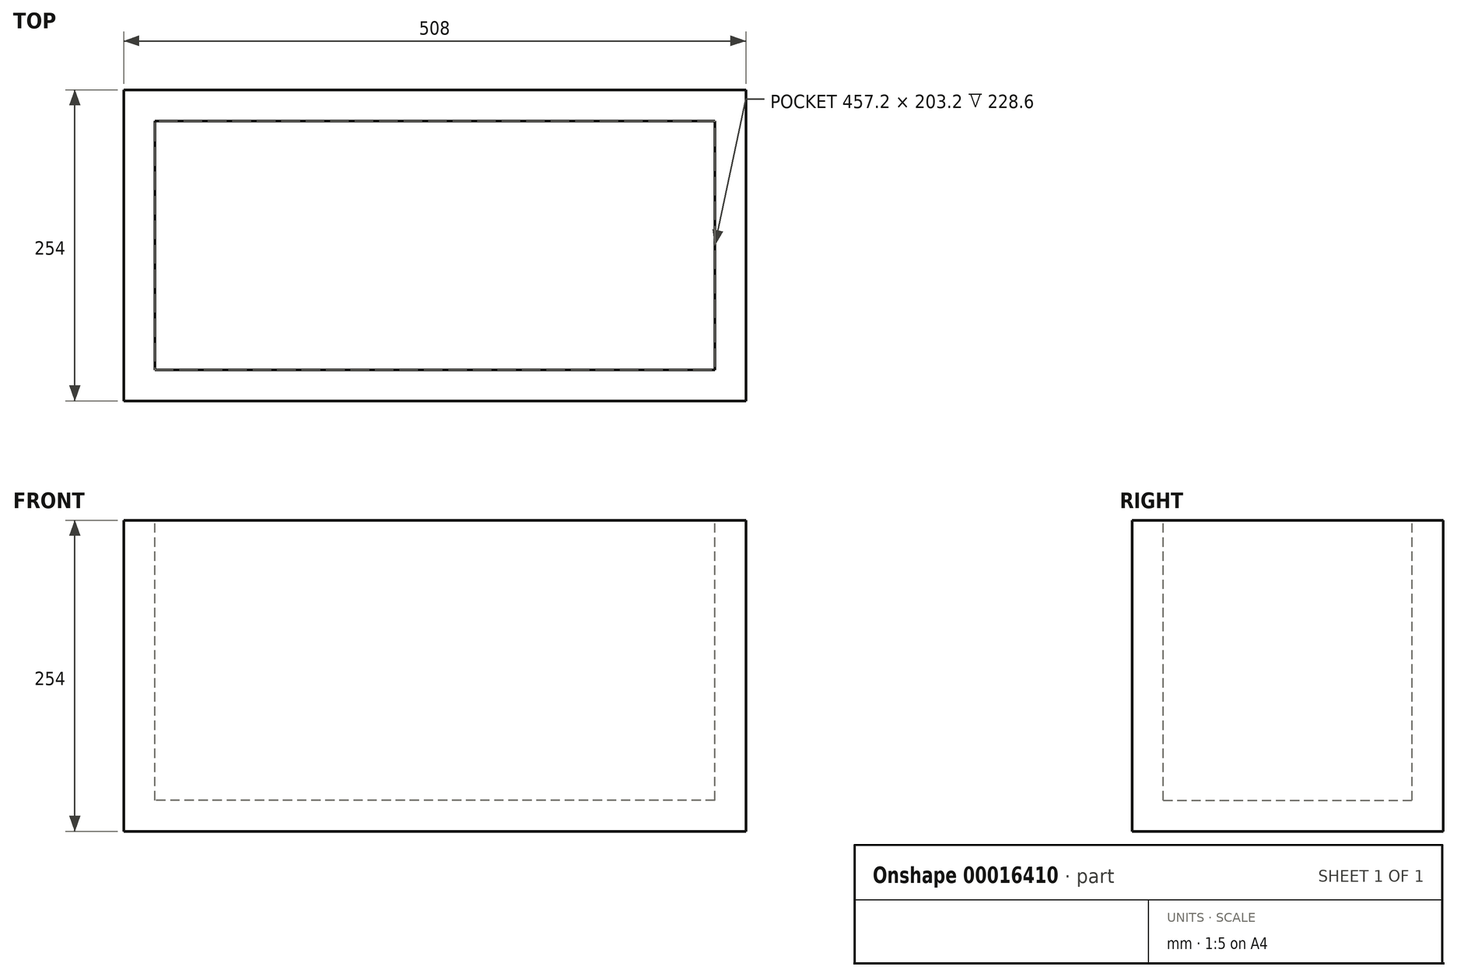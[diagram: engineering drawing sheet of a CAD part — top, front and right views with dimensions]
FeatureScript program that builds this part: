
annotation { "Feature Type Name" : "Feature", "Feature Type Description" : "" }
export const myFeature = defineFeature(function(context is Context, id is Id, definition is map)
    precondition{}
    {
        {
            var Q0;
            Q0=qCreatedBy(makeId("Front.planeOp"),FACE);
            var sketch = newSketch(context, id + "F0", { "sketchPlane" : qUnion([Q0])});
            skLineSegment(sketch, "E0.rect.bottom", {"start": v(443.75, -12.24) * mm, "end": v(-64.25, -12.24) * mm});
            skLineSegment(sketch, "E0.rect.top", {"start": v(443.75, 241.76) * mm, "end": v(-64.25, 241.76) * mm});
            skLineSegment(sketch, "E0.rect.left", {"start": v(443.75, -12.24) * mm, "end": v(443.75, 241.76) * mm});
            skLineSegment(sketch, "E0.rect.right", {"start": v(-64.25, -12.24) * mm, "end": v(-64.25, 241.76) * mm});
            skPoint(sketch, "E0.rect.middle", {"position": v(189.75, 114.76) * mm});
            skSolve(sketch);
        }
        {
            var Q0;
            Q0=makeQuery(id+"F0.imprint","IMPRINT",FACE,{"disambiguationData":[TD([[makeQuery(id+"F0.imprint","IMPRINT",EDGE,{"derivedFrom":sQuery(id+"F0.wireOp",EDGE,"E0.rect.bottom")}),-1.0]])]});
            extrude(context, id + "F1", {"entities" : qUnion([Q0]), "depth" : 254 * mm});
        }
        {
            var Q0;
            Q0=makeQuery(id+"F1.opExtrude","SWEPT_FACE",FACE,{"disambiguationData":[OSD([sQuery(id+"F0.wireOp",EDGE,"E0.rect.top")])]});
            shell(context, id + "F2", {"entities" : qUnion([Q0]), "thickness" : 25.4 * mm});
        }
    });
